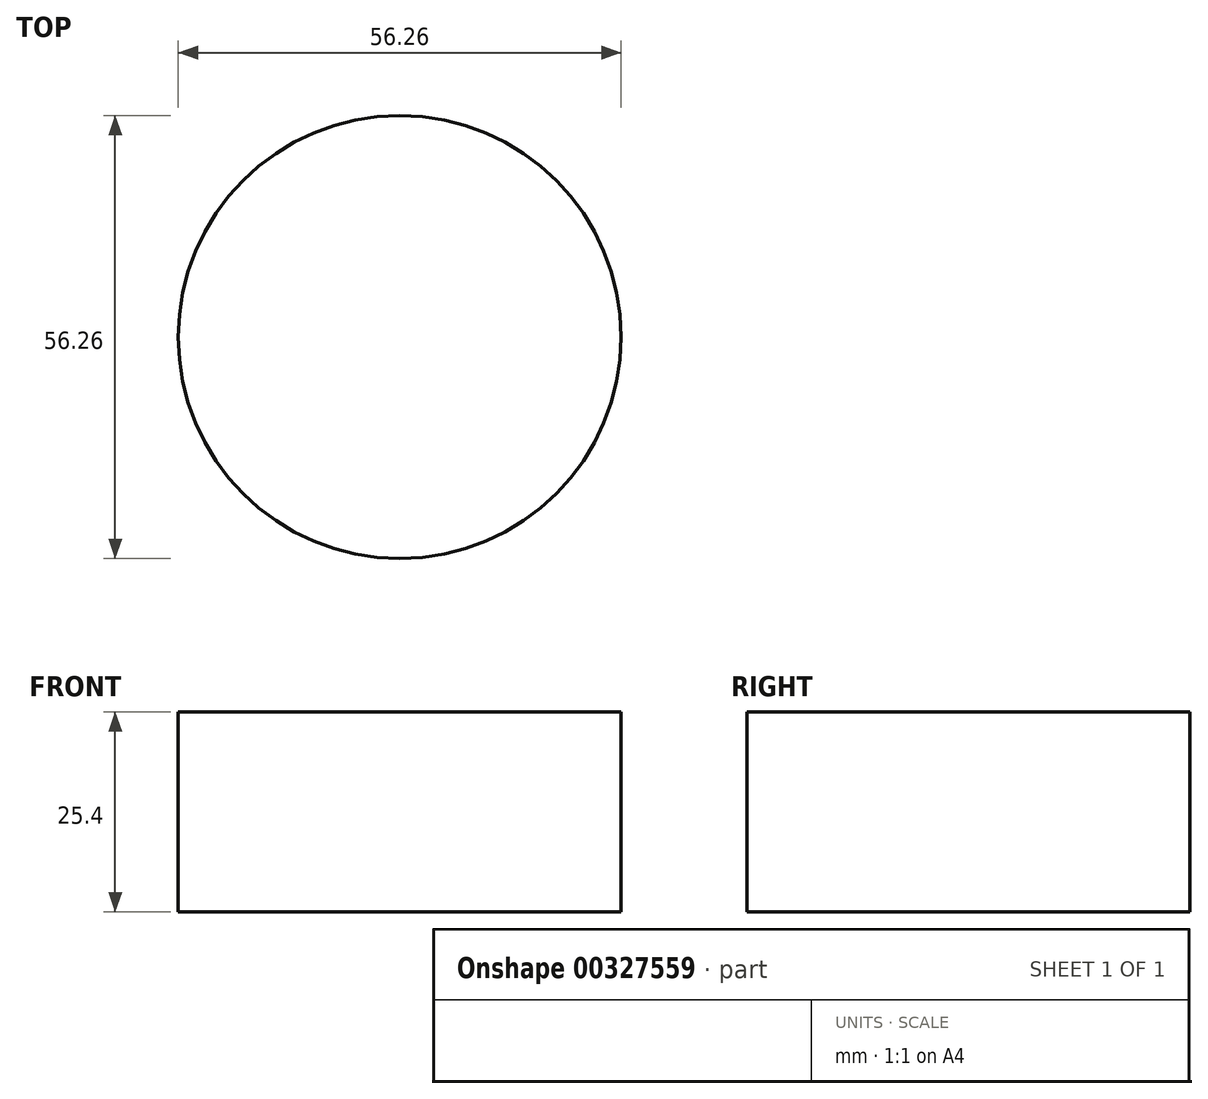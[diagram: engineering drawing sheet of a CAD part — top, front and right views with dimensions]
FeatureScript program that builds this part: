
annotation { "Feature Type Name" : "Feature", "Feature Type Description" : "" }
export const myFeature = defineFeature(function(context is Context, id is Id, definition is map)
    precondition{}
    {
        {
            var Q0;
            Q0=qCreatedBy(makeId("Top.planeOp"),FACE);
            var sketch = newSketch(context, id + "F0", { "sketchPlane" : qUnion([Q0])});
            skCircle(sketch, "E0", {"center": v(-44.52, 40.74) * mm, "radius": 28.13 * mm});
            skSolve(sketch);
        }
        {
            var Q0;
            Q0=makeQuery(id+"F0.imprint","IMPRINT",FACE,{"disambiguationData":[TD([[makeQuery(id+"F0.imprint","IMPRINT",EDGE,{"derivedFrom":sQuery(id+"F0.wireOp",EDGE,"E0")}),1.0]])]});
            var sketch = newSketch(context, id + "F1", { "sketchPlane" : qUnion([Q0])});
            skSolve(sketch);
        }
        {
            var Q0;
            Q0=makeQuery(id+"F1.imprint","IMPRINT",FACE,{"disambiguationData":[TD([[makeQuery(id+"F1.imprint","IMPRINT",EDGE,{"derivedFrom":makeQuery(id+"F0.imprint","IMPRINT",EDGE,{"derivedFrom":sQuery(id+"F0.wireOp",EDGE,"E0")})}),1.0]])]});
            extrude(context, id + "F2", {"entities" : qUnion([Q0]), "depth" : 25.4 * mm});
        }
    });
